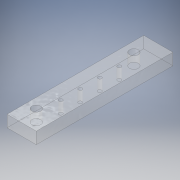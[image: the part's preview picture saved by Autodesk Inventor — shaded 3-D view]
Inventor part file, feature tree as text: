
AUTODESK INVENTOR PART (.ipt)
format: ipt  version: 2019 (Build 230136000, 136)  size: 128,512 bytes
history: native  units: mm
features: extrude x1, sketch x1
ambient origin geometry x8: Origin, YZ Plane, XZ Plane, XY Plane, X Axis, Y Axis, Z Axis, Center Point
bodies: Body1 (feature_tree)
feature tree (2):
  extrude  "Extrusion2"  Depth=15.0mm
  sketch  "Sketch2"  dims[d31=6.0mm d32=0.0mm d76=15.0mm d78=10.0mm d79=50.0mm d80=5.0mm d81=4.5mm d82=10.0mm d83=1.9mm d84=40.0mm d86=10.0mm d87=10.0mm d89=10.0mm d91=10.0mm d92=7.5mm]
